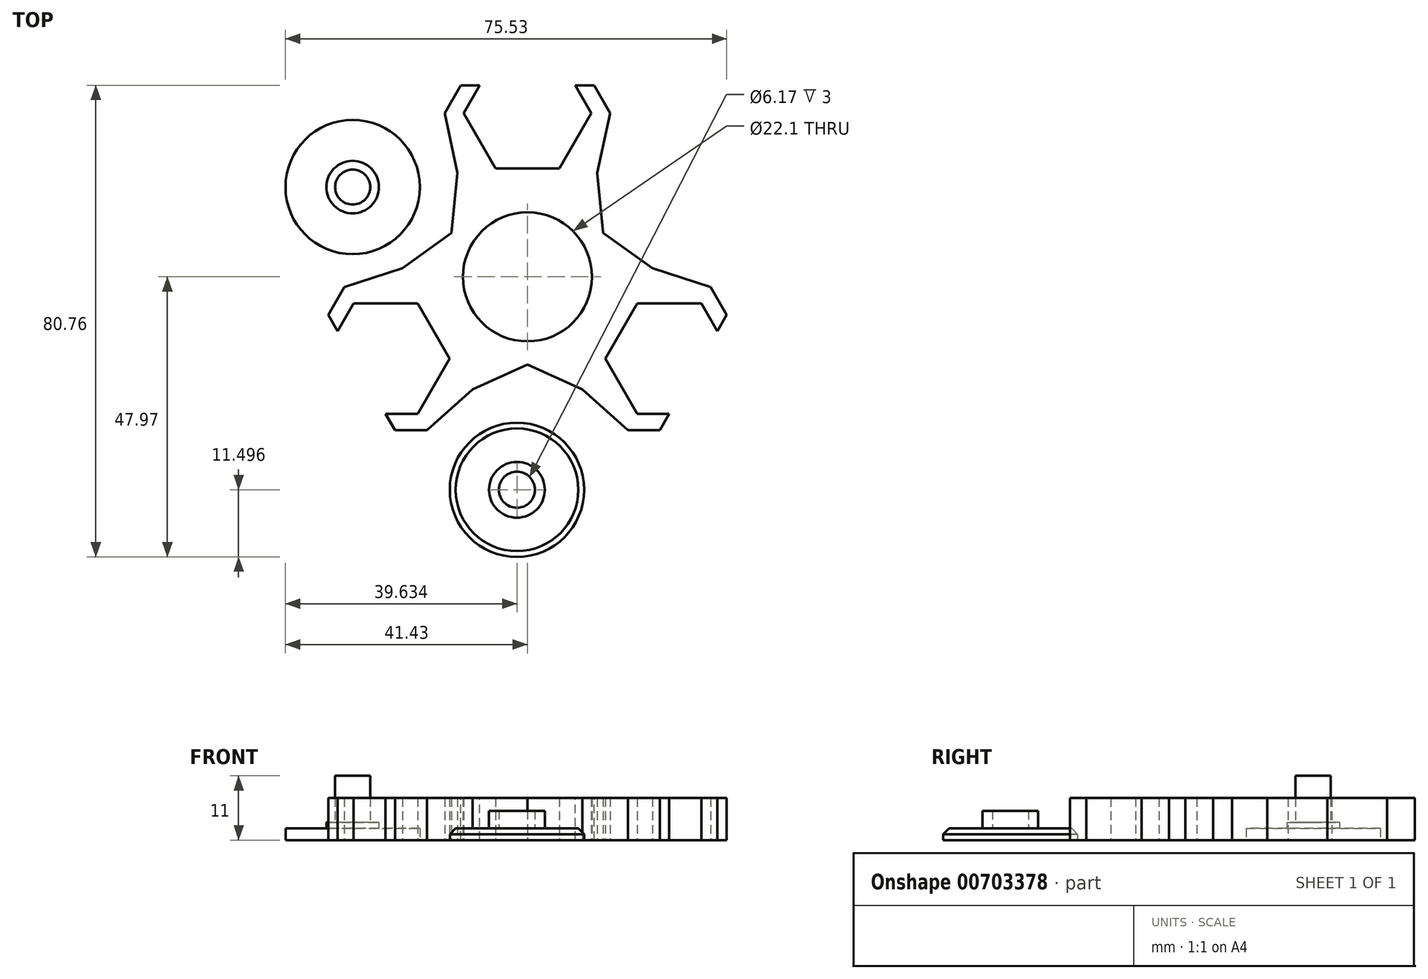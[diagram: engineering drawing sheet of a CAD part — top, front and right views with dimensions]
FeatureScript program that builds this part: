
annotation { "Feature Type Name" : "Feature", "Feature Type Description" : "" }
export const myFeature = defineFeature(function(context is Context, id is Id, definition is map)
    precondition{}
    {
        {
            var Q0;
            Q0=qCreatedBy(makeId("Top.planeOp"),FACE);
            var sketch = newSketch(context, id + "F0", { "sketchPlane" : qUnion([Q0])});
            skCircle(sketch, "E0", {"center": v(0, 0) * mm, "radius": 11.05 * mm});
            skLineSegment(sketch, "E1", {"start": v(0, 11.05) * mm, "end": v(0, 28.05) * mm});
            skCircle(sketch, "E2", {"center": v(0, 28.05) * mm, "radius": 9.47 * mm});
            skLineSegment(sketch, "E3", {"start": v(-9.47, 28.05) * mm, "end": v(9.47, 28.05) * mm});
            skLineSegment(sketch, "E4", {"start": v(0, 37.53) * mm, "end": v(0, 18.57) * mm});
            skCircle(sketch, "E5.cCircle", {"center": v(0, 28.05) * mm, "radius": 9.47 * mm, "construction": true});
            skLineSegment(sketch, "E5.0", {"start": v(5.47, 18.57) * mm, "end": v(-5.47, 18.57) * mm});
            skLineSegment(sketch, "E5.1", {"start": v(-5.47, 18.57) * mm, "end": v(-10.94, 28.05) * mm});
            skLineSegment(sketch, "E5.2", {"start": v(-10.94, 28.05) * mm, "end": v(-5.47, 37.53) * mm});
            skLineSegment(sketch, "E5.3", {"start": v(-5.47, 37.53) * mm, "end": v(5.47, 37.53) * mm});
            skLineSegment(sketch, "E5.4", {"start": v(5.47, 37.52) * mm, "end": v(10.94, 28.05) * mm});
            skLineSegment(sketch, "E5.5", {"start": v(10.94, 28.05) * mm, "end": v(5.47, 18.57) * mm});
            skPoint(sketch, "E5.0.midPoint", {"position": v(0, 18.57) * mm});
            skLineSegment(sketch, "E6", {"start": v(0, 0) * mm, "end": v(9.57, -5.52) * mm});
            skLineSegment(sketch, "E7", {"start": v(0, 0) * mm, "end": v(0, 11.05) * mm});
            skLineSegment(sketch, "E8", {"start": v(0, 0) * mm, "end": v(-9.57, -5.53) * mm});
            skLineSegment(sketch, "E9", {"start": v(9.57, -5.52) * mm, "end": v(24.3, -14.02) * mm});
            skCircle(sketch, "E10", {"center": v(24.3, -14.02) * mm, "radius": 9.47 * mm});
            skCircle(sketch, "E11.cCircle", {"center": v(24.3, -14.02) * mm, "radius": 9.48 * mm, "construction": true});
            skLineSegment(sketch, "E11.0", {"start": v(13.35, -14.02) * mm, "end": v(18.82, -4.55) * mm});
            skLineSegment(sketch, "E11.1", {"start": v(18.82, -4.55) * mm, "end": v(29.76, -4.55) * mm});
            skLineSegment(sketch, "E11.2", {"start": v(29.76, -4.55) * mm, "end": v(35.23, -14.02) * mm});
            skLineSegment(sketch, "E11.3", {"start": v(35.23, -14.02) * mm, "end": v(29.76, -23.5) * mm});
            skLineSegment(sketch, "E11.4", {"start": v(29.76, -23.5) * mm, "end": v(18.82, -23.5) * mm});
            skLineSegment(sketch, "E11.5", {"start": v(18.82, -23.5) * mm, "end": v(13.35, -14.02) * mm});
            skPoint(sketch, "E11.0.midPoint", {"position": v(16.09, -9.29) * mm});
            skLineSegment(sketch, "E12", {"start": v(-9.57, -5.53) * mm, "end": v(-24.3, -14.03) * mm});
            skCircle(sketch, "E13", {"center": v(-24.3, -14.03) * mm, "radius": 9.47 * mm});
            skCircle(sketch, "E14.cCircle", {"center": v(-24.3, -14.03) * mm, "radius": 9.47 * mm, "construction": true});
            skLineSegment(sketch, "E14.0", {"start": v(-18.82, -4.55) * mm, "end": v(-13.35, -14.03) * mm});
            skLineSegment(sketch, "E14.1", {"start": v(-13.35, -14.03) * mm, "end": v(-18.82, -23.5) * mm});
            skLineSegment(sketch, "E14.2", {"start": v(-18.82, -23.5) * mm, "end": v(-29.76, -23.5) * mm});
            skLineSegment(sketch, "E14.3", {"start": v(-29.76, -23.5) * mm, "end": v(-35.23, -14.03) * mm});
            skLineSegment(sketch, "E14.4", {"start": v(-35.23, -14.03) * mm, "end": v(-29.76, -4.55) * mm});
            skLineSegment(sketch, "E14.5", {"start": v(-29.76, -4.55) * mm, "end": v(-18.82, -4.55) * mm});
            skPoint(sketch, "E14.0.midPoint", {"position": v(-16.09, -9.29) * mm});
            skLineSegment(sketch, "E15", {"start": v(0, 0) * mm, "end": v(-13, 7.5) * mm});
            skLineSegment(sketch, "E16", {"start": v(-10.94, 28.05) * mm, "end": v(-13, 7.5) * mm});
            skLineSegment(sketch, "E17", {"start": v(-29.76, -4.55) * mm, "end": v(-13, 7.5) * mm});
            skCircle(sketch, "E18", {"center": v(-24.3, -14.03) * mm, "radius": 12.25 * mm});
            skCircle(sketch, "E19", {"center": v(24.3, -14.02) * mm, "radius": 12.25 * mm});
            skCircle(sketch, "E20", {"center": v(0, 28.05) * mm, "radius": 12.25 * mm});
            skCircle(sketch, "E21.cCircle", {"center": v(0, 28.05) * mm, "radius": 12.25 * mm, "construction": true});
            skLineSegment(sketch, "E21.0", {"start": v(7.07, 15.8) * mm, "end": v(-7.07, 15.8) * mm});
            skLineSegment(sketch, "E21.1", {"start": v(-7.07, 15.8) * mm, "end": v(-14.15, 28.05) * mm});
            skLineSegment(sketch, "E21.2", {"start": v(-14.15, 28.05) * mm, "end": v(-7.07, 40.3) * mm});
            skLineSegment(sketch, "E21.3", {"start": v(-7.07, 40.3) * mm, "end": v(7.07, 40.3) * mm});
            skLineSegment(sketch, "E21.4", {"start": v(7.07, 40.3) * mm, "end": v(14.15, 28.05) * mm});
            skLineSegment(sketch, "E21.5", {"start": v(14.15, 28.05) * mm, "end": v(7.07, 15.8) * mm});
            skPoint(sketch, "E21.0.midPoint", {"position": v(0, 15.8) * mm});
            skCircle(sketch, "E22.cCircle", {"center": v(-24.3, -14.03) * mm, "radius": 12.25 * mm, "construction": true});
            skLineSegment(sketch, "E22.0", {"start": v(-17.22, -1.78) * mm, "end": v(-10.15, -14.03) * mm});
            skLineSegment(sketch, "E22.1", {"start": v(-10.15, -14.03) * mm, "end": v(-17.22, -26.28) * mm});
            skLineSegment(sketch, "E22.2", {"start": v(-17.22, -26.28) * mm, "end": v(-31.36, -26.28) * mm});
            skLineSegment(sketch, "E22.3", {"start": v(-31.36, -26.28) * mm, "end": v(-38.44, -14.03) * mm});
            skLineSegment(sketch, "E22.4", {"start": v(-38.44, -14.03) * mm, "end": v(-31.36, -1.78) * mm});
            skLineSegment(sketch, "E22.5", {"start": v(-31.36, -1.78) * mm, "end": v(-17.22, -1.78) * mm});
            skPoint(sketch, "E22.0.midPoint", {"position": v(-13.68, -7.9) * mm});
            skCircle(sketch, "E23.cCircle", {"center": v(24.3, -14.02) * mm, "radius": 12.25 * mm, "construction": true});
            skLineSegment(sketch, "E23.0", {"start": v(10.15, -14.02) * mm, "end": v(17.22, -1.77) * mm});
            skLineSegment(sketch, "E23.1", {"start": v(17.22, -1.77) * mm, "end": v(31.36, -1.77) * mm});
            skLineSegment(sketch, "E23.2", {"start": v(31.36, -1.77) * mm, "end": v(38.44, -14.02) * mm});
            skLineSegment(sketch, "E23.3", {"start": v(38.44, -14.02) * mm, "end": v(31.36, -26.27) * mm});
            skLineSegment(sketch, "E23.4", {"start": v(31.36, -26.27) * mm, "end": v(17.22, -26.27) * mm});
            skLineSegment(sketch, "E23.5", {"start": v(17.22, -26.27) * mm, "end": v(10.15, -14.02) * mm});
            skPoint(sketch, "E23.0.midPoint", {"position": v(13.68, -7.9) * mm});
            skLineSegment(sketch, "E24", {"start": v(0, 0) * mm, "end": v(13, 7.5) * mm});
            skLineSegment(sketch, "E25", {"start": v(0, 0) * mm, "end": v(0, -15) * mm});
            skLineSegment(sketch, "E26", {"start": v(10.94, 28.05) * mm, "end": v(13, 7.5) * mm});
            skLineSegment(sketch, "E27", {"start": v(29.76, -4.55) * mm, "end": v(13, 7.5) * mm});
            skLineSegment(sketch, "E28", {"start": v(0, -15) * mm, "end": v(18.82, -23.5) * mm});
            skLineSegment(sketch, "E29", {"start": v(-18.82, -23.5) * mm, "end": v(0, -15) * mm});
            skLineSegment(sketch, "E30", {"start": v(-14.15, 28.05) * mm, "end": v(-11.97, 17.77) * mm});
            skLineSegment(sketch, "E31", {"start": v(-31.36, -1.78) * mm, "end": v(-21.38, 1.47) * mm});
            skLineSegment(sketch, "E32", {"start": v(-17.22, -26.28) * mm, "end": v(-9.41, -19.25) * mm});
            skLineSegment(sketch, "E33", {"start": v(17.22, -26.27) * mm, "end": v(9.41, -19.25) * mm});
            skLineSegment(sketch, "E34", {"start": v(31.36, -1.77) * mm, "end": v(21.38, 1.48) * mm});
            skLineSegment(sketch, "E35", {"start": v(14.15, 28.05) * mm, "end": v(11.97, 17.77) * mm});
            skSolve(sketch);
        }
        {
            var Q0;
            {var subQ0=sQuery(id+"F0.wireOp",EDGE,"E16");var subQ1=makeQuery(id+"F0.imprint","INTERSECT",VERTEX,{"derivedFrom":[subQ0,sQuery(id+"F0.wireOp",EDGE,"E30")]});Q0=makeQuery(id+"F0.imprint","IMPRINT",FACE,{"disambiguationData":[TD([[makeQuery(id+"F0.imprint","IMPRINT",EDGE,{"disambiguationData":[TD([[subQ1,1.0]])],"derivedFrom":subQ0}),1.0]])]});}
            var Q1;
            {var subQ0=sQuery(id+"F0.wireOp",EDGE,"E17");var subQ1=makeQuery(id+"F0.imprint","INTERSECT",VERTEX,{"derivedFrom":[subQ0,sQuery(id+"F0.wireOp",EDGE,"E31")]});Q1=makeQuery(id+"F0.imprint","IMPRINT",FACE,{"disambiguationData":[TD([[makeQuery(id+"F0.imprint","IMPRINT",EDGE,{"disambiguationData":[TD([[subQ1,1.0]])],"derivedFrom":subQ0}),-1.0]])]});}
            var Q2;
            {var subQ0=sQuery(id+"F0.wireOp",EDGE,"E22.5");var subQ3=sQuery(id+"F0.wireOp",EDGE,"E22.0");var subQ5=makeQuery(id+"F0.imprint","INTERSECT",VERTEX,{"derivedFrom":[subQ3,subQ0]});Q2=makeQuery(id+"F0.imprint","IMPRINT",FACE,{"disambiguationData":[TD([[makeQuery(id+"F0.imprint","IMPRINT",EDGE,{"disambiguationData":[TD([[subQ5,1.0]])],"derivedFrom":subQ0}),-1.0]])]});}
            var Q3;
            {var subQ0=sQuery(id+"F0.wireOp",EDGE,"E14.5");var subQ1=sQuery(id+"F0.wireOp",EDGE,"E14.0");var subQ2=makeQuery(id+"F0.imprint","INTERSECT",VERTEX,{"derivedFrom":[subQ1,subQ0]});Q3=makeQuery(id+"F0.imprint","IMPRINT",FACE,{"disambiguationData":[TD([[makeQuery(id+"F0.imprint","IMPRINT",EDGE,{"disambiguationData":[TD([[subQ2,1.0]])],"derivedFrom":subQ0}),1.0]])]});}
            var Q4;
            {var subQ0=sQuery(id+"F0.wireOp",EDGE,"E18");var subQ1=sQuery(id+"F0.wireOp",EDGE,"E17");var subQ2=makeQuery(id+"F0.imprint","INTERSECT",VERTEX,{"derivedFrom":[subQ1,subQ0]});Q4=makeQuery(id+"F0.imprint","IMPRINT",FACE,{"disambiguationData":[TD([[makeQuery(id+"F0.imprint","IMPRINT",EDGE,{"disambiguationData":[TD([[subQ2,-1.0]])],"derivedFrom":subQ1}),1.0]])]});}
            var Q5;
            {var subQ0=sQuery(id+"F0.wireOp",EDGE,"E22.4");var subQ1=sQuery(id+"F0.wireOp",EDGE,"E18");var subQ2=makeQuery(id+"F0.imprint","INTERSECT",VERTEX,{"derivedFrom":[subQ1,subQ0]});Q5=makeQuery(id+"F0.imprint","IMPRINT",FACE,{"disambiguationData":[TD([[makeQuery(id+"F0.imprint","IMPRINT",EDGE,{"disambiguationData":[TD([[subQ2,-1.0]])],"derivedFrom":subQ1}),-1.0]])]});}
            var Q6;
            {var subQ9=sQuery(id+"F0.wireOp",EDGE,"E14.3");var subQ13=sQuery(id+"F0.wireOp",EDGE,"E14.2");var subQ17=makeQuery(id+"F0.imprint","INTERSECT",VERTEX,{"derivedFrom":[subQ13,subQ9]});Q6=makeQuery(id+"F0.imprint","IMPRINT",FACE,{"disambiguationData":[TD([[makeQuery(id+"F0.imprint","IMPRINT",EDGE,{"disambiguationData":[TD([[subQ17,1.0]])],"derivedFrom":subQ13}),1.0]])]});}
            var Q7;
            {var subQ0=sQuery(id+"F0.wireOp",EDGE,"E22.3");var subQ1=sQuery(id+"F0.wireOp",EDGE,"E18");var subQ2=makeQuery(id+"F0.imprint","INTERSECT",VERTEX,{"derivedFrom":[subQ1,subQ0]});Q7=makeQuery(id+"F0.imprint","IMPRINT",FACE,{"disambiguationData":[TD([[makeQuery(id+"F0.imprint","IMPRINT",EDGE,{"disambiguationData":[TD([[subQ2,-1.0]])],"derivedFrom":subQ1}),-1.0]])]});}
            var Q8;
            {var subQ0=sQuery(id+"F0.wireOp",EDGE,"E22.2");var subQ1=sQuery(id+"F0.wireOp",EDGE,"E18");var subQ2=makeQuery(id+"F0.imprint","INTERSECT",VERTEX,{"derivedFrom":[subQ1,subQ0]});Q8=makeQuery(id+"F0.imprint","IMPRINT",FACE,{"disambiguationData":[TD([[makeQuery(id+"F0.imprint","IMPRINT",EDGE,{"disambiguationData":[TD([[subQ2,-1.0]])],"derivedFrom":subQ1}),-1.0]])]});}
            var Q9;
            {var subQ0=sQuery(id+"F0.wireOp",EDGE,"E14.1");var subQ1=sQuery(id+"F0.wireOp",EDGE,"E14.0");var subQ2=makeQuery(id+"F0.imprint","INTERSECT",VERTEX,{"derivedFrom":[subQ1,subQ0]});Q9=makeQuery(id+"F0.imprint","IMPRINT",FACE,{"disambiguationData":[TD([[makeQuery(id+"F0.imprint","IMPRINT",EDGE,{"disambiguationData":[TD([[subQ2,-1.0]])],"derivedFrom":subQ0}),1.0]])]});}
            var Q10;
            {var subQ0=sQuery(id+"F0.wireOp",EDGE,"E32");Q10=makeQuery(id+"F0.imprint","IMPRINT",FACE,{"disambiguationData":[TD([[makeQuery(id+"F0.imprint","IMPRINT",EDGE,{"derivedFrom":subQ0}),1.0]])]});}
            var Q11;
            {var subQ0=sQuery(id+"F0.wireOp",EDGE,"E22.1");var subQ1=sQuery(id+"F0.wireOp",EDGE,"E22.0");var subQ2=makeQuery(id+"F0.imprint","INTERSECT",VERTEX,{"derivedFrom":[subQ1,subQ0]});Q11=makeQuery(id+"F0.imprint","IMPRINT",FACE,{"disambiguationData":[TD([[makeQuery(id+"F0.imprint","IMPRINT",EDGE,{"disambiguationData":[TD([[subQ2,-1.0]])],"derivedFrom":subQ0}),1.0]])]});}
            var Q12;
            {var subQ0=sQuery(id+"F0.wireOp",EDGE,"E29");var subQ1=sQuery(id+"F0.wireOp",EDGE,"E18");var subQ2=makeQuery(id+"F0.imprint","INTERSECT",VERTEX,{"derivedFrom":[subQ1,subQ0]});Q12=makeQuery(id+"F0.imprint","IMPRINT",FACE,{"disambiguationData":[TD([[makeQuery(id+"F0.imprint","IMPRINT",EDGE,{"disambiguationData":[TD([[subQ2,-1.0]])],"derivedFrom":subQ1}),-1.0]])]});}
            var Q13;
            {var subQ0=sQuery(id+"F0.wireOp",EDGE,"E18");var subQ1=sQuery(id+"F0.wireOp",EDGE,"E17");var subQ2=makeQuery(id+"F0.imprint","INTERSECT",VERTEX,{"derivedFrom":[subQ1,subQ0]});Q13=makeQuery(id+"F0.imprint","IMPRINT",FACE,{"disambiguationData":[TD([[makeQuery(id+"F0.imprint","IMPRINT",EDGE,{"disambiguationData":[TD([[subQ2,-1.0]])],"derivedFrom":subQ1}),-1.0]])]});}
            var Q14;
            {var subQ0=sQuery(id+"F0.wireOp",EDGE,"E22.1");var subQ3=sQuery(id+"F0.wireOp",EDGE,"E22.0");var subQ5=makeQuery(id+"F0.imprint","INTERSECT",VERTEX,{"derivedFrom":[subQ3,subQ0]});Q14=makeQuery(id+"F0.imprint","IMPRINT",FACE,{"disambiguationData":[TD([[makeQuery(id+"F0.imprint","IMPRINT",EDGE,{"disambiguationData":[TD([[subQ5,-1.0]])],"derivedFrom":subQ0}),-1.0]])]});}
            var Q15;
            {var subQ0=sQuery(id+"F0.wireOp",EDGE,"E23.5");var subQ3=sQuery(id+"F0.wireOp",EDGE,"E19");var subQ8=makeQuery(id+"F0.imprint","INTERSECT",VERTEX,{"derivedFrom":[subQ3,subQ0]});Q15=makeQuery(id+"F0.imprint","IMPRINT",FACE,{"disambiguationData":[TD([[makeQuery(id+"F0.imprint","IMPRINT",EDGE,{"disambiguationData":[TD([[subQ8,1.0]])],"derivedFrom":subQ0}),1.0]])]});}
            var Q16;
            {var subQ0=sQuery(id+"F0.wireOp",EDGE,"E23.1");var subQ1=sQuery(id+"F0.wireOp",EDGE,"E23.0");var subQ2=makeQuery(id+"F0.imprint","INTERSECT",VERTEX,{"derivedFrom":[subQ1,subQ0]});Q16=makeQuery(id+"F0.imprint","IMPRINT",FACE,{"disambiguationData":[TD([[makeQuery(id+"F0.imprint","IMPRINT",EDGE,{"disambiguationData":[TD([[subQ2,-1.0]])],"derivedFrom":subQ0}),1.0]])]});}
            var Q17;
            {var subQ0=sQuery(id+"F0.wireOp",EDGE,"E21.5");var subQ3=sQuery(id+"F0.wireOp",EDGE,"E20");var subQ6=makeQuery(id+"F0.imprint","INTERSECT",VERTEX,{"derivedFrom":[subQ3,subQ0]});Q17=makeQuery(id+"F0.imprint","IMPRINT",FACE,{"disambiguationData":[TD([[makeQuery(id+"F0.imprint","IMPRINT",EDGE,{"disambiguationData":[TD([[subQ6,1.0]])],"derivedFrom":subQ0}),1.0]])]});}
            var Q18;
            {var subQ0=sQuery(id+"F0.wireOp",EDGE,"E23.5");var subQ3=sQuery(id+"F0.wireOp",EDGE,"E23.0");var subQ5=makeQuery(id+"F0.imprint","INTERSECT",VERTEX,{"derivedFrom":[subQ3,subQ0]});Q18=makeQuery(id+"F0.imprint","IMPRINT",FACE,{"disambiguationData":[TD([[makeQuery(id+"F0.imprint","IMPRINT",EDGE,{"disambiguationData":[TD([[subQ5,1.0]])],"derivedFrom":subQ0}),-1.0]])]});}
            var Q19;
            {var subQ0=sQuery(id+"F0.wireOp",EDGE,"E11.5");var subQ1=sQuery(id+"F0.wireOp",EDGE,"E11.0");var subQ2=makeQuery(id+"F0.imprint","INTERSECT",VERTEX,{"derivedFrom":[subQ1,subQ0]});Q19=makeQuery(id+"F0.imprint","IMPRINT",FACE,{"disambiguationData":[TD([[makeQuery(id+"F0.imprint","IMPRINT",EDGE,{"disambiguationData":[TD([[subQ2,1.0]])],"derivedFrom":subQ0}),1.0]])]});}
            var Q20;
            {var subQ0=sQuery(id+"F0.wireOp",EDGE,"E11.1");var subQ1=sQuery(id+"F0.wireOp",EDGE,"E11.0");var subQ2=makeQuery(id+"F0.imprint","INTERSECT",VERTEX,{"derivedFrom":[subQ1,subQ0]});Q20=makeQuery(id+"F0.imprint","IMPRINT",FACE,{"disambiguationData":[TD([[makeQuery(id+"F0.imprint","IMPRINT",EDGE,{"disambiguationData":[TD([[subQ2,-1.0]])],"derivedFrom":subQ0}),1.0]])]});}
            var Q21;
            {var subQ0=sQuery(id+"F0.wireOp",EDGE,"E23.1");var subQ3=sQuery(id+"F0.wireOp",EDGE,"E23.0");var subQ5=makeQuery(id+"F0.imprint","INTERSECT",VERTEX,{"derivedFrom":[subQ3,subQ0]});Q21=makeQuery(id+"F0.imprint","IMPRINT",FACE,{"disambiguationData":[TD([[makeQuery(id+"F0.imprint","IMPRINT",EDGE,{"disambiguationData":[TD([[subQ5,-1.0]])],"derivedFrom":subQ0}),-1.0]])]});}
            var Q22;
            {var subQ0=sQuery(id+"F0.wireOp",EDGE,"E23.5");var subQ1=sQuery(id+"F0.wireOp",EDGE,"E19");var subQ2=makeQuery(id+"F0.imprint","INTERSECT",VERTEX,{"derivedFrom":[subQ1,subQ0]});Q22=makeQuery(id+"F0.imprint","IMPRINT",FACE,{"disambiguationData":[TD([[makeQuery(id+"F0.imprint","IMPRINT",EDGE,{"disambiguationData":[TD([[subQ2,-1.0]])],"derivedFrom":subQ1}),-1.0]])]});}
            var Q23;
            {var subQ0=sQuery(id+"F0.wireOp",EDGE,"E33");Q23=makeQuery(id+"F0.imprint","IMPRINT",FACE,{"disambiguationData":[TD([[makeQuery(id+"F0.imprint","IMPRINT",EDGE,{"derivedFrom":subQ0}),-1.0]])]});}
            var Q24;
            {var subQ0=sQuery(id+"F0.wireOp",EDGE,"E23.4");var subQ1=sQuery(id+"F0.wireOp",EDGE,"E19");var subQ2=makeQuery(id+"F0.imprint","INTERSECT",VERTEX,{"derivedFrom":[subQ1,subQ0]});Q24=makeQuery(id+"F0.imprint","IMPRINT",FACE,{"disambiguationData":[TD([[makeQuery(id+"F0.imprint","IMPRINT",EDGE,{"disambiguationData":[TD([[subQ2,1.0]])],"derivedFrom":subQ1}),-1.0]])]});}
            var Q25;
            {var subQ10=sQuery(id+"F0.wireOp",EDGE,"E11.3");var subQ13=sQuery(id+"F0.wireOp",EDGE,"E11.2");var subQ17=makeQuery(id+"F0.imprint","INTERSECT",VERTEX,{"derivedFrom":[subQ13,subQ10]});Q25=makeQuery(id+"F0.imprint","IMPRINT",FACE,{"disambiguationData":[TD([[makeQuery(id+"F0.imprint","IMPRINT",EDGE,{"disambiguationData":[TD([[subQ17,1.0]])],"derivedFrom":subQ13}),1.0]])]});}
            var Q26;
            {var subQ0=sQuery(id+"F0.wireOp",EDGE,"E23.4");var subQ1=sQuery(id+"F0.wireOp",EDGE,"E19");var subQ2=makeQuery(id+"F0.imprint","INTERSECT",VERTEX,{"derivedFrom":[subQ1,subQ0]});Q26=makeQuery(id+"F0.imprint","IMPRINT",FACE,{"disambiguationData":[TD([[makeQuery(id+"F0.imprint","IMPRINT",EDGE,{"disambiguationData":[TD([[subQ2,-1.0]])],"derivedFrom":subQ1}),-1.0]])]});}
            var Q27;
            {var subQ0=sQuery(id+"F0.wireOp",EDGE,"E23.2");var subQ1=sQuery(id+"F0.wireOp",EDGE,"E19");var subQ2=makeQuery(id+"F0.imprint","INTERSECT",VERTEX,{"derivedFrom":[subQ1,subQ0]});Q27=makeQuery(id+"F0.imprint","IMPRINT",FACE,{"disambiguationData":[TD([[makeQuery(id+"F0.imprint","IMPRINT",EDGE,{"disambiguationData":[TD([[subQ2,1.0]])],"derivedFrom":subQ1}),-1.0]])]});}
            var Q28;
            {var subQ0=sQuery(id+"F0.wireOp",EDGE,"E23.2");var subQ1=sQuery(id+"F0.wireOp",EDGE,"E19");var subQ2=makeQuery(id+"F0.imprint","INTERSECT",VERTEX,{"derivedFrom":[subQ1,subQ0]});Q28=makeQuery(id+"F0.imprint","IMPRINT",FACE,{"disambiguationData":[TD([[makeQuery(id+"F0.imprint","IMPRINT",EDGE,{"disambiguationData":[TD([[subQ2,-1.0]])],"derivedFrom":subQ1}),-1.0]])]});}
            var Q29;
            {var subQ0=sQuery(id+"F0.wireOp",EDGE,"E27");var subQ1=sQuery(id+"F0.wireOp",EDGE,"E19");var subQ2=makeQuery(id+"F0.imprint","INTERSECT",VERTEX,{"derivedFrom":[subQ1,subQ0]});Q29=makeQuery(id+"F0.imprint","IMPRINT",FACE,{"disambiguationData":[TD([[makeQuery(id+"F0.imprint","IMPRINT",EDGE,{"disambiguationData":[TD([[subQ2,-1.0]])],"derivedFrom":subQ1}),-1.0]])]});}
            var Q30;
            {var subQ0=sQuery(id+"F0.wireOp",EDGE,"E31");Q30=makeQuery(id+"F0.imprint","IMPRINT",FACE,{"disambiguationData":[TD([[makeQuery(id+"F0.imprint","IMPRINT",EDGE,{"derivedFrom":subQ0}),-1.0]])]});}
            var Q31;
            {var subQ0=sQuery(id+"F0.wireOp",EDGE,"E34");Q31=makeQuery(id+"F0.imprint","IMPRINT",FACE,{"disambiguationData":[TD([[makeQuery(id+"F0.imprint","IMPRINT",EDGE,{"derivedFrom":subQ0}),1.0]])]});}
            var Q32;
            {var subQ0=sQuery(id+"F0.wireOp",EDGE,"E35");Q32=makeQuery(id+"F0.imprint","IMPRINT",FACE,{"disambiguationData":[TD([[makeQuery(id+"F0.imprint","IMPRINT",EDGE,{"derivedFrom":subQ0}),-1.0]])]});}
            var Q33;
            {var subQ0=sQuery(id+"F0.wireOp",EDGE,"E30");Q33=makeQuery(id+"F0.imprint","IMPRINT",FACE,{"disambiguationData":[TD([[makeQuery(id+"F0.imprint","IMPRINT",EDGE,{"derivedFrom":subQ0}),1.0]])]});}
            var Q34;
            {var subQ1=sQuery(id+"F0.wireOp",EDGE,"E5.1");var subQ5=sQuery(id+"F0.wireOp",EDGE,"E5.0");var subQ8=makeQuery(id+"F0.imprint","INTERSECT",VERTEX,{"derivedFrom":[subQ5,subQ1]});Q34=makeQuery(id+"F0.imprint","IMPRINT",FACE,{"disambiguationData":[TD([[makeQuery(id+"F0.imprint","IMPRINT",EDGE,{"disambiguationData":[TD([[subQ8,-1.0]])],"derivedFrom":subQ1}),1.0]])]});}
            var Q35;
            {var subQ0=sQuery(id+"F0.wireOp",EDGE,"E21.1");var subQ3=sQuery(id+"F0.wireOp",EDGE,"E21.0");var subQ5=makeQuery(id+"F0.imprint","INTERSECT",VERTEX,{"derivedFrom":[subQ3,subQ0]});Q35=makeQuery(id+"F0.imprint","IMPRINT",FACE,{"disambiguationData":[TD([[makeQuery(id+"F0.imprint","IMPRINT",EDGE,{"disambiguationData":[TD([[subQ5,-1.0]])],"derivedFrom":subQ0}),-1.0]])]});}
            var Q36;
            {var subQ0=sQuery(id+"F0.wireOp",EDGE,"E5.5");var subQ1=sQuery(id+"F0.wireOp",EDGE,"E5.0");var subQ2=makeQuery(id+"F0.imprint","INTERSECT",VERTEX,{"derivedFrom":[subQ1,subQ0]});Q36=makeQuery(id+"F0.imprint","IMPRINT",FACE,{"disambiguationData":[TD([[makeQuery(id+"F0.imprint","IMPRINT",EDGE,{"disambiguationData":[TD([[subQ2,1.0]])],"derivedFrom":subQ0}),1.0]])]});}
            var Q37;
            {var subQ0=sQuery(id+"F0.wireOp",EDGE,"E21.5");var subQ3=sQuery(id+"F0.wireOp",EDGE,"E21.0");var subQ5=makeQuery(id+"F0.imprint","INTERSECT",VERTEX,{"derivedFrom":[subQ3,subQ0]});Q37=makeQuery(id+"F0.imprint","IMPRINT",FACE,{"disambiguationData":[TD([[makeQuery(id+"F0.imprint","IMPRINT",EDGE,{"disambiguationData":[TD([[subQ5,1.0]])],"derivedFrom":subQ0}),-1.0]])]});}
            var Q38;
            {var subQ0=sQuery(id+"F0.wireOp",EDGE,"E21.4");var subQ1=sQuery(id+"F0.wireOp",EDGE,"E20");var subQ2=makeQuery(id+"F0.imprint","INTERSECT",VERTEX,{"derivedFrom":[subQ1,subQ0]});Q38=makeQuery(id+"F0.imprint","IMPRINT",FACE,{"disambiguationData":[TD([[makeQuery(id+"F0.imprint","IMPRINT",EDGE,{"disambiguationData":[TD([[subQ2,1.0]])],"derivedFrom":subQ1}),-1.0]])]});}
            var Q39;
            {var subQ1=sQuery(id+"F0.wireOp",EDGE,"E5.2");var subQ10=sQuery(id+"F0.wireOp",EDGE,"E5.3");var subQ16=makeQuery(id+"F0.imprint","INTERSECT",VERTEX,{"derivedFrom":[subQ1,subQ10]});Q39=makeQuery(id+"F0.imprint","IMPRINT",FACE,{"disambiguationData":[TD([[makeQuery(id+"F0.imprint","IMPRINT",EDGE,{"disambiguationData":[TD([[subQ16,1.0]])],"derivedFrom":subQ1}),1.0]])]});}
            var Q40;
            {var subQ0=sQuery(id+"F0.wireOp",EDGE,"E21.3");var subQ1=sQuery(id+"F0.wireOp",EDGE,"E20");var subQ2=makeQuery(id+"F0.imprint","INTERSECT",VERTEX,{"derivedFrom":[subQ1,subQ0]});Q40=makeQuery(id+"F0.imprint","IMPRINT",FACE,{"disambiguationData":[TD([[makeQuery(id+"F0.imprint","IMPRINT",EDGE,{"disambiguationData":[TD([[subQ2,1.0]])],"derivedFrom":subQ1}),-1.0]])]});}
            var Q41;
            {var subQ0=sQuery(id+"F0.wireOp",EDGE,"E21.3");var subQ1=sQuery(id+"F0.wireOp",EDGE,"E20");var subQ2=makeQuery(id+"F0.imprint","INTERSECT",VERTEX,{"derivedFrom":[subQ1,subQ0]});Q41=makeQuery(id+"F0.imprint","IMPRINT",FACE,{"disambiguationData":[TD([[makeQuery(id+"F0.imprint","IMPRINT",EDGE,{"disambiguationData":[TD([[subQ2,-1.0]])],"derivedFrom":subQ1}),-1.0]])]});}
            var Q42;
            {var subQ0=sQuery(id+"F0.wireOp",EDGE,"E20");var subQ1=sQuery(id+"F0.wireOp",EDGE,"E16");var subQ2=makeQuery(id+"F0.imprint","INTERSECT",VERTEX,{"derivedFrom":[subQ1,subQ0]});Q42=makeQuery(id+"F0.imprint","IMPRINT",FACE,{"disambiguationData":[TD([[makeQuery(id+"F0.imprint","IMPRINT",EDGE,{"disambiguationData":[TD([[subQ2,-1.0]])],"derivedFrom":subQ1}),-1.0]])]});}
            var Q43;
            {var subQ0=sQuery(id+"F0.wireOp",EDGE,"E20");var subQ1=sQuery(id+"F0.wireOp",EDGE,"E16");var subQ2=makeQuery(id+"F0.imprint","INTERSECT",VERTEX,{"derivedFrom":[subQ1,subQ0]});Q43=makeQuery(id+"F0.imprint","IMPRINT",FACE,{"disambiguationData":[TD([[makeQuery(id+"F0.imprint","IMPRINT",EDGE,{"disambiguationData":[TD([[subQ2,-1.0]])],"derivedFrom":subQ1}),1.0]])]});}
            var Q44;
            {var subQ0=sQuery(id+"F0.wireOp",EDGE,"E21.5");var subQ1=sQuery(id+"F0.wireOp",EDGE,"E20");var subQ2=makeQuery(id+"F0.imprint","INTERSECT",VERTEX,{"derivedFrom":[subQ1,subQ0]});Q44=makeQuery(id+"F0.imprint","IMPRINT",FACE,{"disambiguationData":[TD([[makeQuery(id+"F0.imprint","IMPRINT",EDGE,{"disambiguationData":[TD([[subQ2,-1.0]])],"derivedFrom":subQ1}),-1.0]])]});}
            extrude(context, id + "F1", {"entities" : qUnion([Q0, Q1, Q2, Q3, Q4, Q5, Q6, Q7, Q8, Q9, Q10, Q11, Q12, Q13, Q14, Q15, Q16, Q17, Q18, Q19, Q20, Q21, Q22, Q23, Q24, Q25, Q26, Q27, Q28, Q29, Q30, Q31, Q32, Q33, Q34, Q35, Q36, Q37, Q38, Q39, Q40, Q41, Q42, Q43, Q44]), "depth" : 7.2 * mm, "offsetDistance" : 25 * mm});
        }
        {
            var Q0;
            Q0=qCreatedBy(makeId("Top.planeOp"),FACE);
            var sketch = newSketch(context, id + "F2", { "sketchPlane" : qUnion([Q0])});
            skCircle(sketch, "E36", {"center": v(-37.3, -49.77) * mm, "radius": 11.5 * mm});
            skCircle(sketch, "E37", {"center": v(-37.3, -49.77) * mm, "radius": 4.78 * mm});
            skCircle(sketch, "E38", {"center": v(-46.93, 47.98) * mm, "radius": 3 * mm});
            skCircle(sketch, "E39", {"center": v(-46.93, 47.98) * mm, "radius": 11.5 * mm});
            skCircle(sketch, "E40", {"center": v(-37.3, -49.77) * mm, "radius": 3.08 * mm});
            skCircle(sketch, "E41", {"center": v(-46.93, 47.98) * mm, "radius": 4.5 * mm});
            skSolve(sketch);
        }
        {
            var Q0;
            Q0=makeQuery(id+"F2.imprint","IMPRINT",FACE,{"disambiguationData":[TD([[makeQuery(id+"F2.imprint","IMPRINT",EDGE,{"derivedFrom":sQuery(id+"F2.wireOp",EDGE,"E36")}),1.0]])]});
            extrude(context, id + "F3", {"entities" : qUnion([Q0]), "depth" : 2 * mm, "offsetDistance" : 25 * mm});
        }
        {
            var Q0;
            Q0=makeQuery(id+"F2.imprint","IMPRINT",FACE,{"disambiguationData":[TD([[makeQuery(id+"F2.imprint","IMPRINT",EDGE,{"derivedFrom":sQuery(id+"F2.wireOp",EDGE,"E37")}),1.0]])]});
            extrude(context, id + "F4", {"entities" : qUnion([Q0]), "operationType" : NewBodyOperationType.ADD, "depth" : 5 * mm, "offsetDistance" : 25 * mm});
        }
        {
            var Q0;
            Q0=makeQuery(id+"F2.imprint","IMPRINT",FACE,{"disambiguationData":[TD([[makeQuery(id+"F2.imprint","IMPRINT",EDGE,{"derivedFrom":sQuery(id+"F2.wireOp",EDGE,"E40")}),1.0]])]});
            extrude(context, id + "F5", {"entities" : qUnion([Q0]), "operationType" : NewBodyOperationType.ADD, "depth" : 2 * mm, "offsetDistance" : 25 * mm});
        }
        {
            var Q0;
            Q0=makeQuery(id+"F2.imprint","IMPRINT",FACE,{"disambiguationData":[TD([[makeQuery(id+"F2.imprint","IMPRINT",EDGE,{"derivedFrom":sQuery(id+"F2.wireOp",EDGE,"E38")}),-1.0]])]});
            extrude(context, id + "F6", {"entities" : qUnion([Q0]), "depth" : 3 * mm, "offsetDistance" : 25 * mm});
        }
        {
            var Q0;
            Q0=makeQuery(id+"F2.imprint","IMPRINT",FACE,{"disambiguationData":[TD([[makeQuery(id+"F2.imprint","IMPRINT",EDGE,{"derivedFrom":sQuery(id+"F2.wireOp",EDGE,"E38")}),1.0]])]});
            extrude(context, id + "F7", {"entities" : qUnion([Q0]), "operationType" : NewBodyOperationType.ADD, "depth" : 11 * mm, "offsetDistance" : 25 * mm});
        }
        {
            var Q0;
            Q0=makeQuery(id+"F2.imprint","IMPRINT",FACE,{"disambiguationData":[TD([[makeQuery(id+"F2.imprint","IMPRINT",EDGE,{"derivedFrom":sQuery(id+"F2.wireOp",EDGE,"E39")}),1.0]])]});
            extrude(context, id + "F8", {"entities" : qUnion([Q0]), "operationType" : NewBodyOperationType.ADD, "depth" : 2 * mm, "offsetDistance" : 25 * mm});
        }
        {
            var Q0;
            Q0=makeQuery(id+"F3.opExtrude","SWEPT_BODY",BODY,{"disambiguationData":[OSD([sQuery(id+"F2.wireOp",EDGE,"E36"),sQuery(id+"F2.wireOp",EDGE,"E37")])]});
            transform(context, id + "F9", {"entities" : qUnion([Q0]), "transformType" : TransformType.TRANSLATION_3D, "dx" : 35.5 * mm, "dy" : 13.3 * mm, "dz" : 0 * mm, "makeCopy" : false});
        }
        {
            var Q0;
            Q0=makeQuery(id+"F6.opExtrude","SWEPT_BODY",BODY,{"disambiguationData":[OSD([sQuery(id+"F2.wireOp",EDGE,"E38"),sQuery(id+"F2.wireOp",EDGE,"E41")])]});
            transform(context, id + "F10", {"entities" : qUnion([Q0]), "transformType" : TransformType.TRANSLATION_3D, "dx" : 17 * mm, "dy" : -32.6 * mm, "dz" : 0 * mm, "makeCopy" : false});
        }
        {
            var Q0;
            Q0=makeQuery(id+"F1.opExtrude","CAP_FACE",FACE,{"disambiguationData":[OSD([sQuery(id+"F0.wireOp",EDGE,"E0"),sQuery(id+"F0.wireOp",EDGE,"E5.0"),sQuery(id+"F0.wireOp",EDGE,"E5.1"),sQuery(id+"F0.wireOp",EDGE,"E5.2"),sQuery(id+"F0.wireOp",EDGE,"E5.3"),sQuery(id+"F0.wireOp",EDGE,"E5.4"),sQuery(id+"F0.wireOp",EDGE,"E5.5"),sQuery(id+"F0.wireOp",EDGE,"E11.0"),sQuery(id+"F0.wireOp",EDGE,"E11.1"),sQuery(id+"F0.wireOp",EDGE,"E11.2"),sQuery(id+"F0.wireOp",EDGE,"E11.3"),sQuery(id+"F0.wireOp",EDGE,"E11.4"),sQuery(id+"F0.wireOp",EDGE,"E11.5"),sQuery(id+"F0.wireOp",EDGE,"E14.0"),sQuery(id+"F0.wireOp",EDGE,"E14.1"),sQuery(id+"F0.wireOp",EDGE,"E14.2"),sQuery(id+"F0.wireOp",EDGE,"E14.3"),sQuery(id+"F0.wireOp",EDGE,"E14.4"),sQuery(id+"F0.wireOp",EDGE,"E14.5"),sQuery(id+"F0.wireOp",EDGE,"E16"),sQuery(id+"F0.wireOp",EDGE,"E17"),sQuery(id+"F0.wireOp",EDGE,"E21.2"),sQuery(id+"F0.wireOp",EDGE,"E21.3"),sQuery(id+"F0.wireOp",EDGE,"E21.4"),sQuery(id+"F0.wireOp",EDGE,"E22.2"),sQuery(id+"F0.wireOp",EDGE,"E22.3"),sQuery(id+"F0.wireOp",EDGE,"E22.4"),sQuery(id+"F0.wireOp",EDGE,"E23.2"),sQuery(id+"F0.wireOp",EDGE,"E23.3"),sQuery(id+"F0.wireOp",EDGE,"E23.4"),sQuery(id+"F0.wireOp",EDGE,"E26"),sQuery(id+"F0.wireOp",EDGE,"E27"),sQuery(id+"F0.wireOp",EDGE,"E28"),sQuery(id+"F0.wireOp",EDGE,"E29"),sQuery(id+"F0.wireOp",EDGE,"E30"),sQuery(id+"F0.wireOp",EDGE,"E31"),sQuery(id+"F0.wireOp",EDGE,"E32"),sQuery(id+"F0.wireOp",EDGE,"E33"),sQuery(id+"F0.wireOp",EDGE,"E34"),sQuery(id+"F0.wireOp",EDGE,"E35")])],"isStart":false});
            var sketch = newSketch(context, id + "F11", { "sketchPlane" : qUnion([Q0])});
            skLineSegment(sketch, "E42", {"start": v(-8.2, 32.79) * mm, "end": v(-11.4, 32.79) * mm});
            skLineSegment(sketch, "E43", {"start": v(-11.4, 32.79) * mm, "end": v(11.4, 32.79) * mm});
            skLineSegment(sketch, "E44", {"start": v(24.3, -23.5) * mm, "end": v(32.5, -9.29) * mm});
            skLineSegment(sketch, "E45", {"start": v(32.5, -9.29) * mm, "end": v(22.69, -26.27) * mm});
            skLineSegment(sketch, "E46", {"start": v(22.69, -26.27) * mm, "end": v(34.1, -6.51) * mm});
            skLineSegment(sketch, "E47", {"start": v(-24.3, -23.5) * mm, "end": v(-32.5, -9.29) * mm});
            skLineSegment(sketch, "E48", {"start": v(-32.5, -9.29) * mm, "end": v(-22.69, -26.28) * mm});
            skLineSegment(sketch, "E49", {"start": v(-22.69, -26.28) * mm, "end": v(-34.1, -6.51) * mm});
            skSolve(sketch);
        }
        {
            var Q0;
            {var subQ2=makeQuery(id+"F1.opExtrude","CAP_EDGE",EDGE,{"disambiguationData":[OSD([sQuery(id+"F0.wireOp",EDGE,"E14.3")])],"isStart":false});Q0=makeQuery(id+"F11.imprint","IMPRINT",FACE,{"disambiguationData":[TD([[makeQuery(id+"F11.imprint","IMPRINT",EDGE,{"derivedFrom":subQ2}),1.0]])]});}
            var Q1;
            {var subQ6=makeQuery(id+"F1.opExtrude","CAP_EDGE",EDGE,{"disambiguationData":[OSD([sQuery(id+"F0.wireOp",EDGE,"E5.3")])],"isStart":false});Q1=makeQuery(id+"F11.imprint","IMPRINT",FACE,{"disambiguationData":[TD([[makeQuery(id+"F11.imprint","IMPRINT",EDGE,{"derivedFrom":subQ6}),1.0]])]});}
            var Q2;
            {var subQ4=makeQuery(id+"F1.opExtrude","CAP_EDGE",EDGE,{"disambiguationData":[OSD([sQuery(id+"F0.wireOp",EDGE,"E11.3")])],"isStart":false});Q2=makeQuery(id+"F11.imprint","IMPRINT",FACE,{"disambiguationData":[TD([[makeQuery(id+"F11.imprint","IMPRINT",EDGE,{"derivedFrom":subQ4}),1.0]])]});}
            extrude(context, id + "F12", {"entities" : qUnion([Q0, Q1, Q2]), "operationType" : NewBodyOperationType.REMOVE, "oppositeDirection" : true, "depth" : 25 * mm, "offsetDistance" : 25 * mm});
        }
        {
            var Q0;
            Q0=makeQuery(id+"F3.opExtrude","CAP_EDGE",EDGE,{"disambiguationData":[OSD([sQuery(id+"F2.wireOp",EDGE,"E36")])],"isStart":false});
            chamfer(context, id + "F13", {"entities" : qUnion([Q0]), "width" : 1 * mm, "tangentPropagation" : true});
        }
    });
